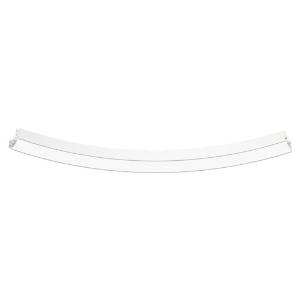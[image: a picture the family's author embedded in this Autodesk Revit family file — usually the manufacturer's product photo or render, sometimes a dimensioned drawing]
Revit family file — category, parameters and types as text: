
# Revit family: super-g_super-g__5400___51deg_ab_led__36_8w_5680lm_3000k_cri_80_350-1160_34fd
name_source: partatom
category: Leuchten
revit_build: Autodesk Revit 2016 (Build: 20190508_0715(x64)
units: mm (PartAtom-declared; Revit-internal decimal feet)

## family parameters
Basisbauteil = Fläche
Beim Laden mit Abzugskörper schneiden = Nein
Bemaßung runder Anschluss = Durchmesser verwenden
Gemeinsam genutzt = Nein
Lichtquelle = Nein
Raumberechnungspunkt = Nein
Teiletyp = Normal

## types (1)
- 350-1160- (1 x LED, 710 lm, 3000K)
    Approval mark = CE
    Beschreibung = The insert consists of aluminum-extruded profile. Charming SOFT-EDGE design ensure unparalleled styling. The ballast is integrated and allows for an operation with 220-240V (50/60Hz). SUPER-G (# 350-1160) ist not dimmable (on/off).
    CIE Flux Codes = 44 75 94 100 65
    Color Rendering = 1B/80…89
    Color Temperature = 3000K
    Height = 120 mm
    Hersteller = Prolicht
    Lamp Light Flux = 710 lm
    Lamp count = 1
    Lampe = 1 x LED
    Length = 300 mm
    Luminous efficacy = 90 lm/W
    ModVariant = Nein
    Modell = 350-1160
    Mounting Place = Ceiling
    Mounting Type = Surface mounted
    Number of Poles = 1
    OnlyDefault = Ja
    Power Factor = 1
    Product Name = SUPER-G__SUPER-G  5400 / 51° AB LED: 36,8W 5680lm 3000K CRI:80
    Product group = Surface profile systems
    ProductGroupID = 335
    Protection Class = Protection class I
    Protection Degree = IP 20
    RLX_Detail_Level = 1
    RlxData = <blob elided: 27713 chars, md5=3fc6851d>
    Scheinlast = 41 VA
    Socket = socket
    Standby Power = 0 W
    System Light Flux = 3692 lm
    System Power = 41 W
    Typenbild = 350-1160.jpg
    URL = http://relux.com
    VarID = 350-1160-
    Voltage = 0 V
    Vorgabe-Ansicht = 1800 mm
    Weight = 0.00 kg
    Width = 150 mm

## geometry (parser evidence)
native form markers: Blend x4, Sweep x27
no freeform markers — native parametric forms only
